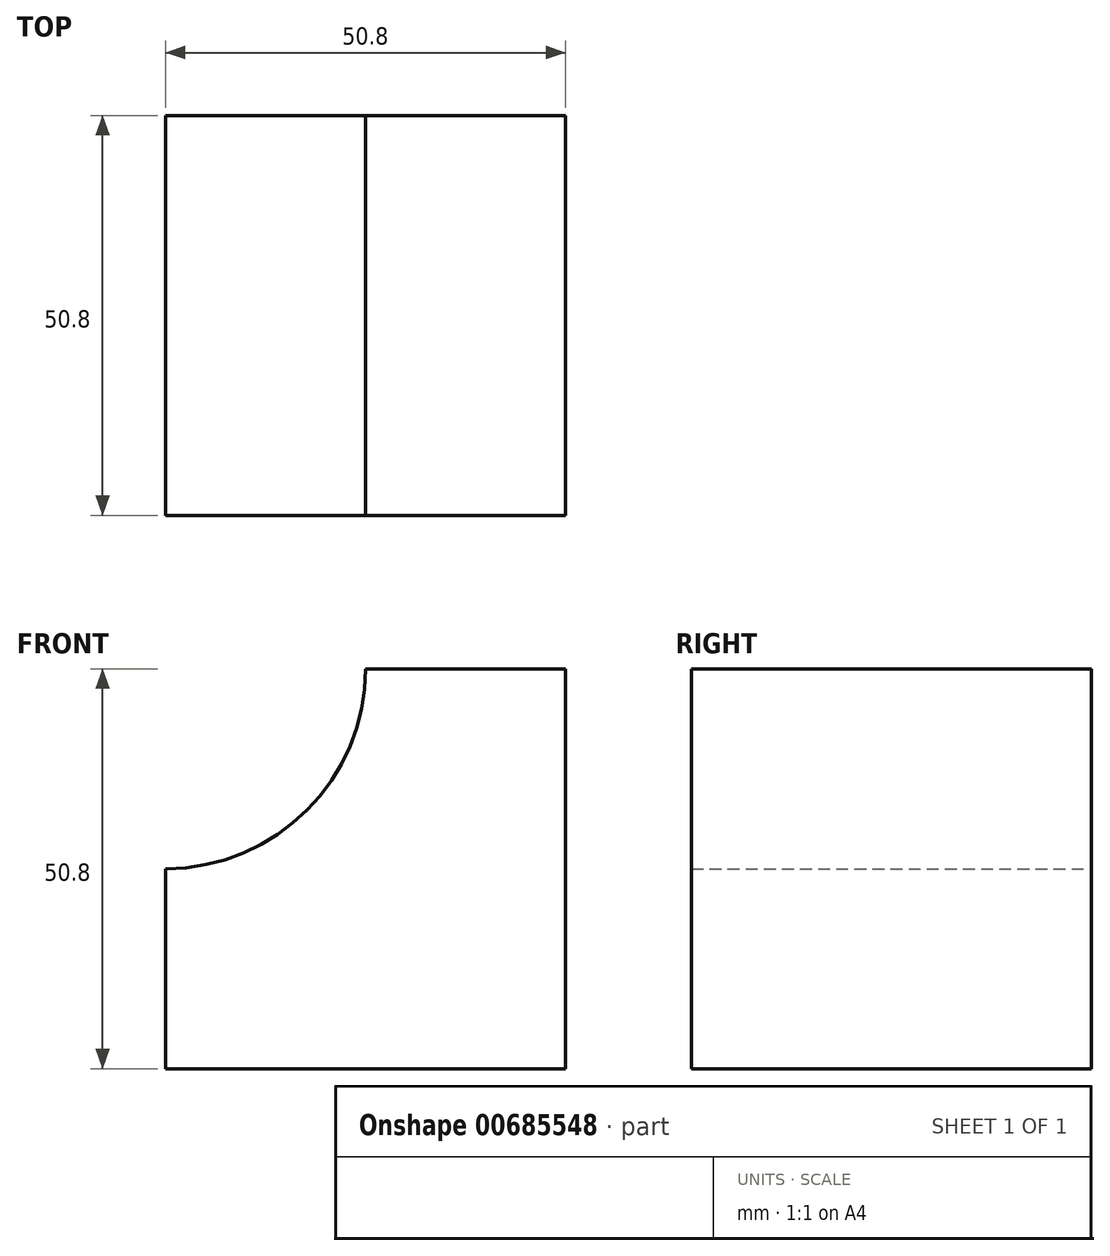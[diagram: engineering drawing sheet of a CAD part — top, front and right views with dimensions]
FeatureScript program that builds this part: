
annotation { "Feature Type Name" : "Feature", "Feature Type Description" : "" }
export const myFeature = defineFeature(function(context is Context, id is Id, definition is map)
    precondition{}
    {
        {
            var Q0;
            Q0=qCreatedBy(makeId("Front.planeOp"),FACE);
            var sketch = newSketch(context, id + "F0", { "sketchPlane" : qUnion([Q0])});
            skLineSegment(sketch, "E0", {"start": v(0, 0) * mm, "end": v(0, 50.8) * mm});
            skLineSegment(sketch, "E1", {"start": v(0, 50.8) * mm, "end": v(-25.4, 50.8) * mm});
            skLineSegment(sketch, "E2", {"start": v(0, 0) * mm, "end": v(-50.8, 0) * mm});
            skLineSegment(sketch, "E3", {"start": v(-50.8, 0) * mm, "end": v(-50.8, 25.4) * mm});
            skArc(sketch, "E4", {"start": v(-50.8, 25.4) * mm, "mid": v(-32.84, 32.84) * mm, "end": v(-25.4, 50.8) * mm});
            skSolve(sketch);
        }
        {
            var Q0;
            Q0 = qSketchRegion(id + "F0", true);
            extrude(context, id + "F1", {"entities" : qUnion([Q0]), "depth" : 50.8 * mm, "offsetDistance" : 25.4 * mm});
        }
    });
